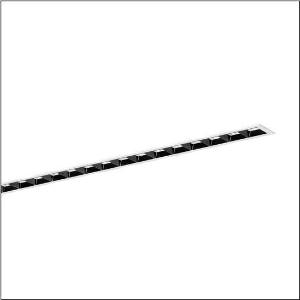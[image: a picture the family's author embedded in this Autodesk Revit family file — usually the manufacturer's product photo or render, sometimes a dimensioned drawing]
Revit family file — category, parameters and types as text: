
# Revit family: silica_r__21_51mx11da44wb_a581
name_source: partatom
category: Lighting Fixtures
units: mm (PartAtom-declared; Revit-internal decimal feet)

## family parameters
Cut with Voids When Loaded = No
Host = Face
Light Source = No
Part Type = Normal
Room Calculation Point = No
Round Connector Dimension = Use Diameter
Shared = No

## types (1)
- --- (1 x LED, 4320 lm, 25.6 W, 4000K)
    Apparent Load = 26 VA
    CIE Flux Codes = 87 99 100 100 100
    Color Rendering = 80
    Color Temperature = 4000K
    Default Elevation = 1800 mm
    Description = Silica® 21, office luminaire, primary light control with darklight reflector, of PMMA, black, CAT 2 (L<= 3000cd/m²), light emission: direct distribution, primary light characteristic: symmetric, installation type: recessed, LED, rated luminous flux: 4.320lm, luminous efficacy: 169lm/W, light colour: 840, colour temperature: 4000K, with terminal, 3+2-pole, max. 2.5mm², mains connection: 220..240V, AC, 50/60Hz, rated input power: 25.6W, luminaire housing, of aluminium, traffic white (RAL 9016), length: 1.228mm, width: 79mm, height: 53mm, protection rating (complete): IP20, insulation class (complete): insulation class I (protective earthing), certification: CE, permissible operating ambient temperature: 0..+35°C, standard: EN 50419, packaging unit: 1 piece
    Height = 0 mm  [stored 0 ft]
    Lamp = 1 x LED
    Lamp Light Flux = 4320 lm
    Lamp Power = 25.6 W
    Lamp count = 1
    Length = 1227 mm
    Luminous efficacy = 169 lm/W
    Manufacturer = Siteco
    ModVariant = No
    Model = 51MX11DA44WB
    Mounting Place = Ceiling
    Mounting Type = Recessed
    Number of Poles = 1
    OnlyDefault = Yes
    Power Factor = 1
    Product Name = Silica® 21
    Product group = office luminaire | ceiling recessed
    ProductGroupID = 401
    Protection Class = Protection class I
    Protection Degree = IP 20
    RLX_Detail_Level = 1
    RLX_Emergency_Light_Flux = 0 lm
    RLX_Emergency_Type = 0
    RLX_Emergency_Type_DB = No
    RlxData = <blob elided: 38649 chars, md5=bd983bc1>
    Socket = socket
    Standby Power = 0 W
    System Light Flux = 4320 lm
    System Power = 26 W
    Type Comments = factory setting: luminous flux: 100 % | dim-lin: 254 | 367 mA
    Type Image = l_1297791.jpg
    URL = http://relux.com
    VarID = @adj_054233
    Voltage = 0 V
    Weight = 0.00 kg
    Width = 79 mm

note: [stored X ft] marks values corroborated as IEEE doubles in the binary element streams (Revit-internal decimal feet)

## geometry (parser evidence)
native form markers: Blend x4, Sweep x12
no freeform markers — native parametric forms only
